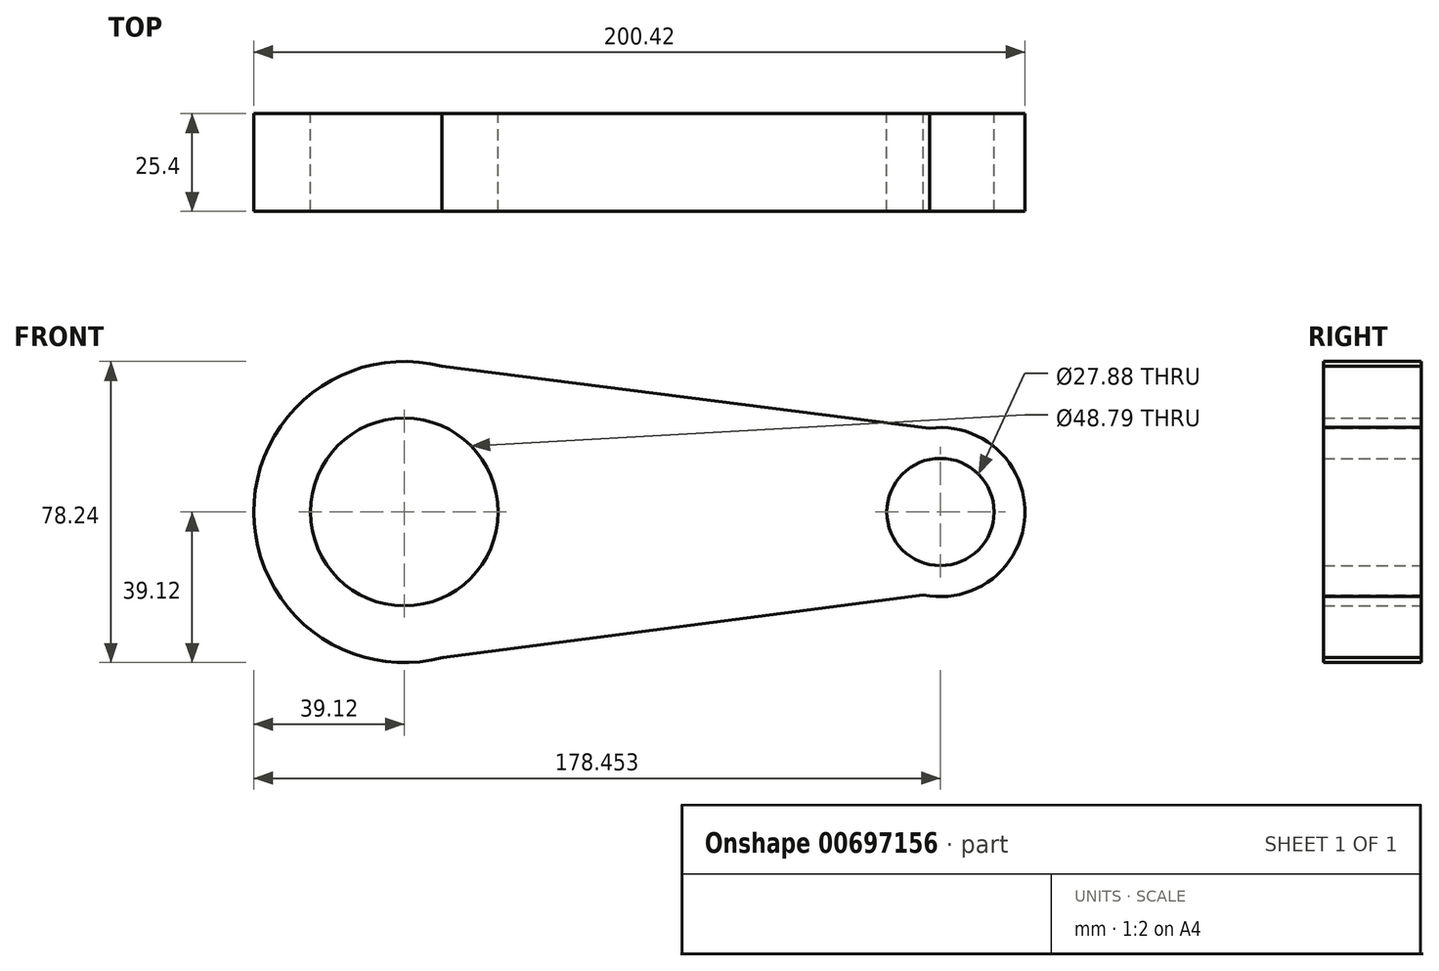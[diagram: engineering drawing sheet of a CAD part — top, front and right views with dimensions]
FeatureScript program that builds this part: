
annotation { "Feature Type Name" : "Feature", "Feature Type Description" : "" }
export const myFeature = defineFeature(function(context is Context, id is Id, definition is map)
    precondition{}
    {
        {
            var Q0;
            Q0=qCreatedBy(makeId("Front.planeOp"),FACE);
            var sketch = newSketch(context, id + "F0", { "sketchPlane" : qUnion([Q0])});
            skCircle(sketch, "E0", {"center": v(0, 0) * mm, "radius": 39.12 * mm});
            skCircle(sketch, "E1", {"center": v(139.33, 0) * mm, "radius": 21.97 * mm});
            skLineSegment(sketch, "E2", {"start": v(0, 39.12) * mm, "end": v(136.5, 21.79) * mm});
            skLineSegment(sketch, "E3", {"start": v(0, -39.12) * mm, "end": v(134.9, -21.52) * mm});
            skCircle(sketch, "E4", {"center": v(139.33, 0) * mm, "radius": 13.94 * mm});
            skCircle(sketch, "E5", {"center": v(0, 0) * mm, "radius": 24.4 * mm});
            skSolve(sketch);
        }
        {
            var Q0;
            Q0 = qSketchRegion(id + "F0", true);
            extrude(context, id + "F1", {"entities" : qUnion([Q0]), "depth" : 25.4 * mm, "offsetDistance" : 25.4 * mm});
        }
    });
